# Revit family: RWLT-VNE_LOD_400
name_source: partatom
category: Equipement de génie climatique
revit_build: Autodesk Revit 2016 (Build: 20150220_1215(x64)
units: mm (PartAtom-declared; Revit-internal decimal feet)

## family parameters
Cote de connecteur circulaire = Utiliser le diamètre
Couper avec des vides une fois chargée = Non
Hôte = Face
Numéro OmniClass = 23.75.00.00
Partagée = Non
Point de calcul de pièce = Non
Titre OmniClass = Climate Control (HVAC)
Type d'élément = Normal

## types (3) — shared parameters
Color = Pure white (RAL 9010)
Description = Hydro Free Low Temperature - RWLT
Elévation par défaut = 1219.20 mm
Fabricant = HITACHI
Frequency = 50 Hz
Height of pipes = 35.00 mm
Liquid Diameter = 9.52 mm
Mass = 44.00 kg
Maximum AC Voltage = 253 V
Maximum allowable water pressure = 300000.0 Pa
Minimum AC Voltage = 207 V
Minimum allowable water pressure = 100000.0 Pa
Modèle = Hydro Free Low Temperature - RWLT
Nominal Voltage = 230 V
Number of Poles = 1
Operation and service space = Oui
Operation and service space a = 150.00 mm
Operation and service space b = 100.00 mm
Refrigerant = R410A
Running current with DHW tank = 13 A
Unloaded Weight = 35.00 kg

## per-type parameters (varying)
| type | Cooling Operation (Water Inlet 12° Water outlet 7°) | Cooling Operation (Water Inlet 23° Water outlet 18°) | Diamètre Eau Sortie | Distance WID | Distance WOD | Distance gas pipe | Distance liquide pipe | Gas Diameter | Heating Operation (Water Inlet 30° Water outlet 35°C) (OAT 7°C) | Heating Operation (Water Inlet 40° Water outlet 45°C) (OAT 7°C) | Inlet Water Diameter | Maximum water flow rate | Minimum installationwater volume | Minimum water flow rate (Cooling) | Minimum water flow rate (Heating) | Nominal water flow (Water inlet 30°C Water outlet 35°C) | Overall Depth | Overall Height | Overall Width | Sound power at rated load (dB(A)) | Usage Current |
| RWLT-3.0VNE | 21 kW | 27 kW | 25.00 mm | 45.00 mm | 138.00 mm | 264.00 mm | 208.50 mm | 15.88 mm | 31 kW | 31 kW | 25.00 mm | 4.6 m³/h | 180.0 L | 2.5 m³/h | 2.3 m³/h | 4.1 m³/h | 275.00 mm | 712.00 mm | 450.00 mm | 37 | 1 A |
| RWLT-5.0VNE | 13 kW | 16 kW | 32.00 mm | 49.00 mm | 134.00 mm | 265.00 mm | 211.00 mm | 15.88 mm | 16 kW | 15 kW | 32.00 mm | 3.0 m³/h | 150.0 L | 1.5 m³/h | 1.3 m³/h | 2.4 m³/h | 360.00 mm | 890.00 mm | 520.00 mm | 39 | 0 A |
| RWLT-10.0VNE | 21 kW | 27 kW | 32.00 mm | 49.00 mm | 134.00 mm | 265.00 mm | 211.00 mm | 22.20 mm | 31 kW | 31 kW | 32.00 mm | 4.6 m³/h | 180.0 L | 2.5 m³/h | 2.3 m³/h | 4.1 m³/h | 360.00 mm | 890.00 mm | 670.00 mm | 47 | 1 A |

note: column(s) folded — value = type name in every type: Commentaires du type

## geometry (parser evidence)
native form markers: Blend x2
no freeform markers — native parametric forms only
